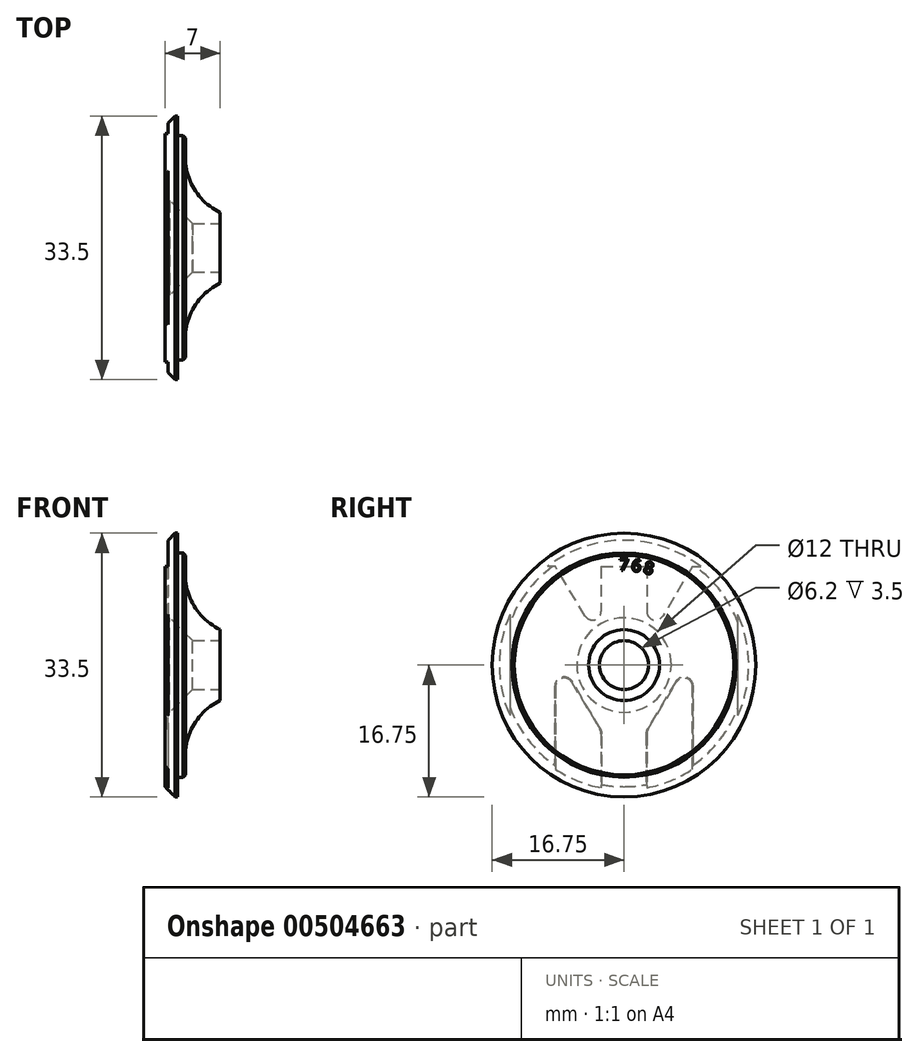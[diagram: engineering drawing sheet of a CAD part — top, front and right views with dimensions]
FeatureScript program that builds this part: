
annotation { "Feature Type Name" : "Feature", "Feature Type Description" : "" }
export const myFeature = defineFeature(function(context is Context, id is Id, definition is map)
    precondition{}
    {
        {
            var Q0;
            Q0=qCreatedBy(makeId("Top.planeOp"),FACE);
            var sketch = newSketch(context, id + "F0", { "sketchPlane" : qUnion([Q0])});
            skLineSegment(sketch, "E0", {"start": v(-4.4, 14.25) * mm, "end": v(-5.4, 14.25) * mm});
            skLineSegment(sketch, "E1", {"start": v(-5.4, 14.25) * mm, "end": v(-5.4, 16.75) * mm});
            skLineSegment(sketch, "E2", {"start": v(0, 0) * mm, "end": v(-7, 0) * mm, "construction": true});
            skLineSegment(sketch, "E3", {"start": v(-3.5, 3.1) * mm, "end": v(0, 3.1) * mm});
            skLineSegment(sketch, "E4", {"start": v(0, 3.1) * mm, "end": v(0, 4.5) * mm});
            skLineSegment(sketch, "E5", {"start": v(-5.4, 16.75) * mm, "end": v(-7, 16.75) * mm});
            skLineSegment(sketch, "E6", {"start": v(-7, 6) * mm, "end": v(-7, 16.75) * mm});
            skLineSegment(sketch, "E7", {"start": v(-6.4, 6) * mm, "end": v(-3.5, 3.1) * mm});
            skLineSegment(sketch, "E8", {"start": v(-7, 6) * mm, "end": v(-6.4, 6) * mm});
            skLineSegment(sketch, "E9", {"start": v(-4.4, 14.25) * mm, "end": v(-4.4, 11.5) * mm});
            skArc(sketch, "E10", {"start": v(-4.4, 11.5) * mm, "mid": v(-3.2, 7.37) * mm, "end": v(0, 4.5) * mm});
            skSolve(sketch);
        }
        {
            var Q0;
            Q0=makeQuery(id+"F0.imprint","IMPRINT",FACE,{"disambiguationData":[TD([[makeQuery(id+"F0.imprint","IMPRINT",EDGE,{"derivedFrom":sQuery(id+"F0.wireOp",EDGE,"E0")}),1.0]])]});
            var Q1;
            Q1=sQuery(id+"F0.wireOp",EDGE,"E2");
            revolve(context, id + "F1", {"entities" : qUnion([Q0]), "axis" : qUnion([Q1]), "revolveType" : RevolveType.FULL});
        }
        {
            var Q0;
            Q0=makeQuery(id+"F1.opRevolve","SWEPT_EDGE",EDGE,{"disambiguationData":[OSD([sQuery(id+"F0.wireOp",EDGE,"E5"),sQuery(id+"F0.wireOp",EDGE,"E6")])]});
            chamfer(context, id + "F2", {"entities" : qUnion([Q0]), "width" : 1.3 * mm, "tangentPropagation" : true});
        }
        {
            var Q0;
            Q0=makeQuery(id+"F1.opRevolve","SWEPT_FACE",FACE,{"disambiguationData":[OSD([sQuery(id+"F0.wireOp",EDGE,"E6")])]});
            var sketch = newSketch(context, id + "F3", { "sketchPlane" : qUnion([Q0])});
            skCircle(sketch, "E11", {"center": v(0, 0) * mm, "radius": 16.75 * mm});
            skLineSegment(sketch, "E12", {"start": v(-2.9, 12.5) * mm, "end": v(-2.9, -16.5) * mm});
            skLineSegment(sketch, "E13.MirrorCS", {"start": v(2.9, 12.5) * mm, "end": v(2.9, -16.5) * mm});
            skLineSegment(sketch, "E14", {"start": v(-8.7, -14.31) * mm, "end": v(-8.7, 1.24) * mm});
            skLineSegment(sketch, "E15", {"start": v(-8.7, 1.24) * mm, "end": v(-2.9, -8.41) * mm});
            skLineSegment(sketch, "E16", {"start": v(2.9, -8.41) * mm, "end": v(8.7, 1.24) * mm});
            skLineSegment(sketch, "E17", {"start": v(8.7, 1.24) * mm, "end": v(8.7, -14.31) * mm});
            skLineSegment(sketch, "E18", {"start": v(-14.5, -8.39) * mm, "end": v(-14.5, 8.39) * mm});
            skLineSegment(sketch, "E19", {"start": v(-8.7, 12.5) * mm, "end": v(-2.9, 2.85) * mm});
            skLineSegment(sketch, "E20", {"start": v(2.9, 2.85) * mm, "end": v(8.7, 12.5) * mm});
            skLineSegment(sketch, "E21", {"start": v(14.5, 8.39) * mm, "end": v(14.5, -8.39) * mm});
            skLineSegment(sketch, "E22", {"start": v(0, 16.75) * mm, "end": v(0, -16.75) * mm, "construction": true});
            skLineSegment(sketch, "E23", {"start": v(2.9, 12.5) * mm, "end": v(-2.9, 12.5) * mm});
            skLineSegment(sketch, "E24", {"start": v(8.7, 1.24) * mm, "end": v(14.5, 1.24) * mm, "construction": true});
            skLineSegment(sketch, "E25", {"start": v(-8.7, 1.24) * mm, "end": v(-14.5, 1.24) * mm, "construction": true});
            skLineSegment(sketch, "E26", {"start": v(-2.9, 2.85) * mm, "end": v(-7.87, -0.14) * mm, "construction": true});
            skLineSegment(sketch, "E27", {"start": v(2.9, -8.41) * mm, "end": v(8.7, -8.41) * mm, "construction": true});
            skLineSegment(sketch, "E28", {"start": v(-8.7, 12.5) * mm, "end": v(-11.15, 12.5) * mm});
            skLineSegment(sketch, "E29", {"start": v(8.7, 12.5) * mm, "end": v(11.15, 12.5) * mm});
            skArc(sketch, "E30", {"start": v(-4.94, 6.25) * mm, "mid": v(-3.7, 5.75) * mm, "end": v(-2.9, 6.81) * mm});
            skArc(sketch, "E31", {"start": v(2.9, 6.81) * mm, "mid": v(3.7, 5.75) * mm, "end": v(4.94, 6.25) * mm});
            skCircle(sketch, "E32.0", {"center": v(0, 0) * mm, "radius": 6 * mm, "construction": true});
            skLineSegment(sketch, "E33", {"start": v(8.7, -11.87) * mm, "end": v(14.5, -11.87) * mm, "construction": true});
            skSolve(sketch);
        }
        {
            var Q0;
            {var subQ8=sQuery(id+"F3.wireOp",EDGE,"E23");Q0=makeQuery(id+"F3.imprint","IMPRINT",FACE,{"disambiguationData":[TD([[makeQuery(id+"F3.imprint","IMPRINT",EDGE,{"derivedFrom":subQ8}),-1.0]])]});}
            var Q1;
            {var subQ0=sQuery(id+"F3.wireOp",EDGE,"E15");Q1=makeQuery(id+"F3.imprint","IMPRINT",FACE,{"disambiguationData":[TD([[makeQuery(id+"F3.imprint","IMPRINT",EDGE,{"derivedFrom":subQ0}),-1.0]])]});}
            var Q2;
            {var subQ0=sQuery(id+"F3.wireOp",EDGE,"E16");Q2=makeQuery(id+"F3.imprint","IMPRINT",FACE,{"disambiguationData":[TD([[makeQuery(id+"F3.imprint","IMPRINT",EDGE,{"derivedFrom":subQ0}),-1.0]])]});}
            var Q3;
            {var subQ0=sQuery(id+"F3.wireOp",EDGE,"E21");var subQ1=sQuery(id+"F0.wireOp",EDGE,"E6");var subQ2=makeQuery(id+"F2.opChamfer","BLEND_EDGE",EDGE,{"blendedFrom":[makeQuery(id+"F1.opRevolve","SWEPT_EDGE",EDGE,{"disambiguationData":[OSD([sQuery(id+"F0.wireOp",EDGE,"E5"),subQ1])]}),makeQuery(id+"F1.opRevolve","SWEPT_FACE",FACE,{"disambiguationData":[OSD([subQ1])]})],"blendedInto":[makeQuery(id+"F1.opRevolve","SWEPT_FACE",FACE,{"disambiguationData":[OSD([subQ1])]})]});var subQ3=makeQuery(id+"F3.imprint","INTERSECT",VERTEX,{"disambiguationData":[OD(0.0)],"derivedFrom":[subQ2,subQ0]});Q3=makeQuery(id+"F3.imprint","IMPRINT",FACE,{"disambiguationData":[TD([[makeQuery(id+"F3.imprint","IMPRINT",EDGE,{"disambiguationData":[TD([[subQ3,-1.0]])],"derivedFrom":subQ0}),1.0]])]});}
            var Q4;
            {var subQ0=sQuery(id+"F3.wireOp",EDGE,"E21");var subQ1=sQuery(id+"F3.wireOp",EDGE,"E11");var subQ2=makeQuery(id+"F3.imprint","INTERSECT",VERTEX,{"disambiguationData":[OD(0.0)],"derivedFrom":[subQ1,subQ0]});Q4=makeQuery(id+"F3.imprint","IMPRINT",FACE,{"disambiguationData":[TD([[makeQuery(id+"F3.imprint","IMPRINT",EDGE,{"disambiguationData":[TD([[subQ2,1.0]])],"derivedFrom":subQ1}),1.0]])]});}
            var Q5;
            {var subQ0=sQuery(id+"F3.wireOp",EDGE,"E18");var subQ1=sQuery(id+"F0.wireOp",EDGE,"E6");var subQ2=makeQuery(id+"F2.opChamfer","BLEND_EDGE",EDGE,{"blendedFrom":[makeQuery(id+"F1.opRevolve","SWEPT_EDGE",EDGE,{"disambiguationData":[OSD([sQuery(id+"F0.wireOp",EDGE,"E5"),subQ1])]}),makeQuery(id+"F1.opRevolve","SWEPT_FACE",FACE,{"disambiguationData":[OSD([subQ1])]})],"blendedInto":[makeQuery(id+"F1.opRevolve","SWEPT_FACE",FACE,{"disambiguationData":[OSD([subQ1])]})]});var subQ3=makeQuery(id+"F3.imprint","INTERSECT",VERTEX,{"disambiguationData":[OD(0.0)],"derivedFrom":[subQ2,subQ0]});Q5=makeQuery(id+"F3.imprint","IMPRINT",FACE,{"disambiguationData":[TD([[makeQuery(id+"F3.imprint","IMPRINT",EDGE,{"disambiguationData":[TD([[subQ3,-1.0]])],"derivedFrom":subQ0}),1.0]])]});}
            var Q6;
            {var subQ0=sQuery(id+"F3.wireOp",EDGE,"E18");var subQ1=sQuery(id+"F3.wireOp",EDGE,"E11");var subQ2=makeQuery(id+"F3.imprint","INTERSECT",VERTEX,{"disambiguationData":[OD(0.0)],"derivedFrom":[subQ1,subQ0]});Q6=makeQuery(id+"F3.imprint","IMPRINT",FACE,{"disambiguationData":[TD([[makeQuery(id+"F3.imprint","IMPRINT",EDGE,{"disambiguationData":[TD([[subQ2,1.0]])],"derivedFrom":subQ1}),1.0]])]});}
            var Q7;
            {var subQ0=sQuery(id+"F3.wireOp",EDGE,"E28");var subQ1=sQuery(id+"F3.wireOp",EDGE,"E11");var subQ2=makeQuery(id+"F3.imprint","INTERSECT",VERTEX,{"derivedFrom":[subQ1,subQ0]});Q7=makeQuery(id+"F3.imprint","IMPRINT",FACE,{"disambiguationData":[TD([[makeQuery(id+"F3.imprint","IMPRINT",EDGE,{"disambiguationData":[TD([[subQ2,1.0]])],"derivedFrom":subQ1}),1.0]])]});}
            var Q8;
            {var subQ0=sQuery(id+"F3.wireOp",EDGE,"E12");var subQ1=sQuery(id+"F3.wireOp",EDGE,"E11");var subQ2=makeQuery(id+"F3.imprint","INTERSECT",VERTEX,{"derivedFrom":[subQ1,subQ0]});Q8=makeQuery(id+"F3.imprint","IMPRINT",FACE,{"disambiguationData":[TD([[makeQuery(id+"F3.imprint","IMPRINT",EDGE,{"disambiguationData":[TD([[subQ2,1.0]])],"derivedFrom":subQ1}),1.0]])]});}
            var Q9;
            {var subQ0=sQuery(id+"F3.wireOp",EDGE,"E13.MirrorCS");var subQ1=sQuery(id+"F3.wireOp",EDGE,"E11");var subQ2=makeQuery(id+"F3.imprint","INTERSECT",VERTEX,{"derivedFrom":[subQ1,subQ0]});Q9=makeQuery(id+"F3.imprint","IMPRINT",FACE,{"disambiguationData":[TD([[makeQuery(id+"F3.imprint","IMPRINT",EDGE,{"disambiguationData":[TD([[subQ2,-1.0]])],"derivedFrom":subQ1}),1.0]])]});}
            extrude(context, id + "F4", {"entities" : qUnion([Q0, Q1, Q2, Q3, Q4, Q5, Q6, Q7, Q8, Q9]), "operationType" : NewBodyOperationType.REMOVE, "oppositeDirection" : true, "depth" : 0.4 * mm, "offsetDistance" : 25 * mm});
        }
        {
            var Q0;
            Q0=makeQuery(id+"F4.boolean.opBoolean","COPY",EDGE,{"derivedFrom":makeQuery(id+"F4.opExtrude","SWEPT_EDGE",EDGE,{"disambiguationData":[OSD([sQuery(id+"F3.wireOp",EDGE,"E14"),sQuery(id+"F3.wireOp",EDGE,"E15")])]})});
            var Q1;
            Q1=makeQuery(id+"F4.boolean.opBoolean","COPY",EDGE,{"derivedFrom":makeQuery(id+"F4.opExtrude","SWEPT_EDGE",EDGE,{"disambiguationData":[OSD([sQuery(id+"F3.wireOp",EDGE,"E16"),sQuery(id+"F3.wireOp",EDGE,"E17")])]})});
            var Q2;
            Q2=makeQuery(id+"F4.boolean.opBoolean","COPY",EDGE,{"derivedFrom":makeQuery(id+"F4.opExtrude","SWEPT_EDGE",EDGE,{"disambiguationData":[OSD([sQuery(id+"F3.wireOp",EDGE,"E12"),sQuery(id+"F3.wireOp",EDGE,"E15")])]})});
            var Q3;
            Q3=makeQuery(id+"F4.boolean.opBoolean","COPY",EDGE,{"derivedFrom":makeQuery(id+"F4.opExtrude","SWEPT_EDGE",EDGE,{"disambiguationData":[OSD([sQuery(id+"F3.wireOp",EDGE,"E13.MirrorCS"),sQuery(id+"F3.wireOp",EDGE,"E16")])]})});
            fillet(context, id + "F5", {"entities" : qUnion([Q0, Q1, Q2, Q3]), "radius" : 1.1 * mm, "tangentPropagation" : true, "allowEdgeOverflow" : false});
        }
        {
            var Q0;
            Q0=makeQuery(id+"F1.opRevolve","SWEPT_FACE",FACE,{"disambiguationData":[OSD([sQuery(id+"F0.wireOp",EDGE,"E9")])]});
            var sketch = newSketch(context, id + "F6", { "sketchPlane" : qUnion([Q0])});
            skCircle(sketch, "E34", {"center": v(0, 0) * mm, "radius": 12 * mm, "construction": true});
            skCircle(sketch, "E35.cCircle", {"center": v(0, 0) * mm, "radius": 11.98 * mm, "construction": true});
            skLineSegment(sketch, "E35.0", {"start": v(-2.98, -11.62) * mm, "end": v(-4.42, -11.16) * mm});
            skLineSegment(sketch, "E35.1", {"start": v(-4.42, -11.16) * mm, "end": v(-5.78, -10.52) * mm});
            skLineSegment(sketch, "E35.2", {"start": v(-5.78, -10.52) * mm, "end": v(-7.05, -9.7) * mm});
            skLineSegment(sketch, "E35.3", {"start": v(-7.05, -9.7) * mm, "end": v(-8.21, -8.75) * mm});
            skLineSegment(sketch, "E35.4", {"start": v(-8.21, -8.75) * mm, "end": v(-9.25, -7.65) * mm});
            skLineSegment(sketch, "E35.5", {"start": v(-9.25, -7.65) * mm, "end": v(-10.13, -6.43) * mm});
            skLineSegment(sketch, "E35.6", {"start": v(-10.13, -6.43) * mm, "end": v(-10.86, -5.1) * mm});
            skLineSegment(sketch, "E35.7", {"start": v(-10.86, -5.1) * mm, "end": v(-11.41, -3.7) * mm});
            skLineSegment(sketch, "E35.8", {"start": v(-11.41, -3.7) * mm, "end": v(-11.79, -2.25) * mm});
            skLineSegment(sketch, "E35.9", {"start": v(-11.79, -2.25) * mm, "end": v(-11.98, -0.75) * mm});
            skLineSegment(sketch, "E35.10", {"start": v(-11.98, -0.75) * mm, "end": v(-11.98, 0.75) * mm});
            skLineSegment(sketch, "E35.11", {"start": v(-11.98, 0.75) * mm, "end": v(-11.79, 2.25) * mm});
            skLineSegment(sketch, "E35.12", {"start": v(-11.79, 2.25) * mm, "end": v(-11.41, 3.7) * mm});
            skLineSegment(sketch, "E35.13", {"start": v(-11.41, 3.7) * mm, "end": v(-10.86, 5.1) * mm});
            skLineSegment(sketch, "E35.14", {"start": v(-10.86, 5.1) * mm, "end": v(-10.13, 6.43) * mm});
            skLineSegment(sketch, "E35.15", {"start": v(-10.13, 6.43) * mm, "end": v(-9.25, 7.65) * mm});
            skLineSegment(sketch, "E35.16", {"start": v(-9.25, 7.65) * mm, "end": v(-8.21, 8.75) * mm});
            skLineSegment(sketch, "E35.17", {"start": v(-8.21, 8.75) * mm, "end": v(-7.05, 9.7) * mm});
            skLineSegment(sketch, "E35.18", {"start": v(-7.05, 9.7) * mm, "end": v(-5.78, 10.52) * mm});
            skLineSegment(sketch, "E35.19", {"start": v(-5.78, 10.52) * mm, "end": v(-4.42, 11.16) * mm});
            skLineSegment(sketch, "E35.20", {"start": v(-4.42, 11.16) * mm, "end": v(-2.98, 11.62) * mm});
            skLineSegment(sketch, "E35.21", {"start": v(-2.98, 11.62) * mm, "end": v(-1.5, 11.9) * mm});
            skLineSegment(sketch, "E35.22", {"start": v(-1.5, 11.9) * mm, "end": v(0, 12) * mm});
            skLineSegment(sketch, "E35.23", {"start": v(0, 12) * mm, "end": v(1.5, 11.9) * mm});
            skLineSegment(sketch, "E35.24", {"start": v(1.5, 11.9) * mm, "end": v(2.98, 11.62) * mm});
            skLineSegment(sketch, "E35.25", {"start": v(2.98, 11.62) * mm, "end": v(4.42, 11.16) * mm});
            skLineSegment(sketch, "E35.26", {"start": v(4.42, 11.16) * mm, "end": v(5.78, 10.52) * mm});
            skLineSegment(sketch, "E35.27", {"start": v(5.78, 10.52) * mm, "end": v(7.05, 9.7) * mm});
            skLineSegment(sketch, "E35.28", {"start": v(7.05, 9.7) * mm, "end": v(8.21, 8.75) * mm});
            skLineSegment(sketch, "E35.29", {"start": v(8.21, 8.75) * mm, "end": v(9.25, 7.65) * mm});
            skLineSegment(sketch, "E35.30", {"start": v(9.25, 7.65) * mm, "end": v(10.13, 6.43) * mm});
            skLineSegment(sketch, "E35.31", {"start": v(10.13, 6.43) * mm, "end": v(10.86, 5.1) * mm});
            skLineSegment(sketch, "E35.32", {"start": v(10.86, 5.1) * mm, "end": v(11.41, 3.7) * mm});
            skLineSegment(sketch, "E35.33", {"start": v(11.41, 3.7) * mm, "end": v(11.79, 2.25) * mm});
            skLineSegment(sketch, "E35.34", {"start": v(11.79, 2.25) * mm, "end": v(11.98, 0.75) * mm});
            skLineSegment(sketch, "E35.35", {"start": v(11.98, 0.75) * mm, "end": v(11.98, -0.75) * mm});
            skLineSegment(sketch, "E35.36", {"start": v(11.98, -0.75) * mm, "end": v(11.79, -2.25) * mm});
            skLineSegment(sketch, "E35.37", {"start": v(11.79, -2.25) * mm, "end": v(11.41, -3.7) * mm});
            skLineSegment(sketch, "E35.38", {"start": v(11.41, -3.7) * mm, "end": v(10.86, -5.1) * mm});
            skLineSegment(sketch, "E35.39", {"start": v(10.86, -5.1) * mm, "end": v(10.13, -6.43) * mm});
            skLineSegment(sketch, "E35.40", {"start": v(10.13, -6.43) * mm, "end": v(9.25, -7.65) * mm});
            skLineSegment(sketch, "E35.41", {"start": v(9.25, -7.65) * mm, "end": v(8.21, -8.75) * mm});
            skLineSegment(sketch, "E35.42", {"start": v(8.21, -8.75) * mm, "end": v(7.05, -9.7) * mm});
            skLineSegment(sketch, "E35.43", {"start": v(7.05, -9.7) * mm, "end": v(5.78, -10.52) * mm});
            skLineSegment(sketch, "E35.44", {"start": v(5.78, -10.52) * mm, "end": v(4.42, -11.16) * mm});
            skLineSegment(sketch, "E35.45", {"start": v(4.42, -11.16) * mm, "end": v(2.98, -11.62) * mm});
            skLineSegment(sketch, "E35.46", {"start": v(2.98, -11.62) * mm, "end": v(1.5, -11.9) * mm});
            skLineSegment(sketch, "E35.47", {"start": v(1.5, -11.9) * mm, "end": v(0, -12) * mm});
            skLineSegment(sketch, "E35.48", {"start": v(0, -12) * mm, "end": v(-1.5, -11.9) * mm});
            skLineSegment(sketch, "E35.49", {"start": v(-1.5, -11.9) * mm, "end": v(-2.98, -11.62) * mm});
            skPoint(sketch, "E35.0.midPoint", {"position": v(-3.7, -11.4) * mm});
            skLineSegment(sketch, "E36", {"start": v(0, 0) * mm, "end": v(0, 12) * mm, "construction": true});
            skLineSegment(sketch, "E37", {"start": v(0, 0) * mm, "end": v(1.5, 11.9) * mm, "construction": true});
            skLineSegment(sketch, "E38", {"start": v(0, 0) * mm, "end": v(2.98, 11.62) * mm, "construction": true});
            skText(sketch, "E39", { "text": "7", "fontName": "OpenSans-Regular.ttf"});
            skText(sketch, "E40", { "text": "8", "fontName": "OpenSans-Regular.ttf"});
            skText(sketch, "E41", { "text": "6", "fontName": "OpenSans-Regular.ttf"});
            skText(sketch, "E42", { "text": "-", "fontName": "OpenSans-Regular.ttf"});
            skLineSegment(sketch, "E43", {"start": v(0, 0) * mm, "end": v(5.78, 10.52) * mm, "construction": true});
            skLineSegment(sketch, "E44", {"start": v(8.21, 8.75) * mm, "end": v(0, 0) * mm, "construction": true});
            skCircle(sketch, "E45.0", {"center": v(0, 0) * mm, "radius": 11.5 * mm, "construction": true});
            skCircle(sketch, "E46.0", {"center": v(0, 0) * mm, "radius": 14.25 * mm, "construction": true});
            const initialGuessF6  = {"E39": [-0.00061, 0.012, 1, 0, 0.0015], "E40": [0.0024, 0.01177, 0.96858, -0.24869, 0.0015], "E41": [0.0009, 0.01198, 0.99211, -0.12533, 0.0015], "E42": [0.00547, 0.01069, 0.8763, -0.48175, 0.0015]};
            skSetInitialGuess(sketch, initialGuessF6);
            skSolve(sketch);
        }
        {
            var Q0;
            Q0=makeQuery(id+"F6.imprint","IMPRINT",FACE,{"disambiguationData":[TD([[makeQuery(id+"F6.imprint","IMPRINT",EDGE,{"derivedFrom":sQuery(id+"F6.wireOp",EDGE,"E39.sketch_text.stroke-0")}),-1.0]])]});
            var Q1;
            Q1=makeQuery(id+"F6.imprint","IMPRINT",FACE,{"disambiguationData":[TD([[makeQuery(id+"F6.imprint","IMPRINT",EDGE,{"derivedFrom":sQuery(id+"F6.wireOp",EDGE,"E41.sketch_text.stroke-0")}),-1.0]])]});
            var Q2;
            Q2=makeQuery(id+"F6.imprint","IMPRINT",FACE,{"disambiguationData":[TD([[makeQuery(id+"F6.imprint","IMPRINT",EDGE,{"derivedFrom":sQuery(id+"F6.wireOp",EDGE,"E40.sketch_text.stroke-0")}),-1.0]])]});
            extrude(context, id + "F7", {"entities" : qUnion([Q0, Q1, Q2]), "operationType" : NewBodyOperationType.REMOVE, "oppositeDirection" : true, "depth" : 0.05 * mm, "offsetDistance" : 25 * mm});
        }
        {
            var Q0;
            Q0=makeQuery(id+"F1.opRevolve","SWEPT_EDGE",EDGE,{"disambiguationData":[OSD([sQuery(id+"F0.wireOp",EDGE,"E0"),sQuery(id+"F0.wireOp",EDGE,"E9")])]});
            chamfer(context, id + "F8", {"entities" : qUnion([Q0]), "width" : 0.3 * mm, "tangentPropagation" : true});
        }
        {
            var Q0;
            Q0=makeQuery(id+"F4.boolean.opBoolean","COPY",EDGE,{"derivedFrom":makeQuery(id+"F4.opExtrude","CAP_EDGE",EDGE,{"disambiguationData":[OSD([sQuery(id+"F3.wireOp",EDGE,"E14")])],"isStart":true})});
            var Q1;
            Q1=makeQuery(id+"F5.opFillet","BLEND_EDGE",EDGE,{"blendedFrom":[makeQuery(id+"F4.boolean.opBoolean","COPY",EDGE,{"derivedFrom":makeQuery(id+"F4.opExtrude","SWEPT_EDGE",EDGE,{"disambiguationData":[OSD([sQuery(id+"F3.wireOp",EDGE,"E14"),sQuery(id+"F3.wireOp",EDGE,"E15")])]})}),makeQuery(id+"F1.opRevolve","SWEPT_FACE",FACE,{"disambiguationData":[OSD([sQuery(id+"F0.wireOp",EDGE,"E6")])]})],"blendedInto":[makeQuery(id+"F1.opRevolve","SWEPT_FACE",FACE,{"disambiguationData":[OSD([sQuery(id+"F0.wireOp",EDGE,"E6")])]})]});
            var Q2;
            {var subQ0=sQuery(id+"F3.wireOp",EDGE,"E13.MirrorCS");Q2=makeQuery(id+"F4.boolean.opBoolean","COPY",EDGE,{"derivedFrom":makeQuery(id+"F4.opExtrude","CAP_EDGE",EDGE,{"disambiguationData":[OSD([subQ0]),TDD([makeQuery(id+"F3.imprint","IMPRINT",EDGE,{"disambiguationData":[TD([[makeQuery(id+"F3.imprint","INTERSECT",VERTEX,{"derivedFrom":[subQ0,sQuery(id+"F3.wireOp",EDGE,"E16")]}),-1.0]])],"derivedFrom":subQ0}),makeQuery(id+"F3.imprint","IMPRINT",EDGE,{"disambiguationData":[TD([[makeQuery(id+"F3.imprint","INTERSECT",VERTEX,{"derivedFrom":[sQuery(id+"F3.wireOp",EDGE,"E11"),subQ0]}),1.0]])],"derivedFrom":subQ0})])],"isStart":true})});}
            var Q3;
            Q3=makeQuery(id+"F5.opFillet","BLEND_EDGE",EDGE,{"blendedFrom":[makeQuery(id+"F4.boolean.opBoolean","COPY",EDGE,{"derivedFrom":makeQuery(id+"F4.opExtrude","SWEPT_EDGE",EDGE,{"disambiguationData":[OSD([sQuery(id+"F3.wireOp",EDGE,"E13.MirrorCS"),sQuery(id+"F3.wireOp",EDGE,"E16")])]})}),makeQuery(id+"F1.opRevolve","SWEPT_FACE",FACE,{"disambiguationData":[OSD([sQuery(id+"F0.wireOp",EDGE,"E6")])]})],"blendedInto":[makeQuery(id+"F1.opRevolve","SWEPT_FACE",FACE,{"disambiguationData":[OSD([sQuery(id+"F0.wireOp",EDGE,"E6")])]})]});
            var Q4;
            Q4=makeQuery(id+"F4.boolean.opBoolean","COPY",EDGE,{"derivedFrom":makeQuery(id+"F4.opExtrude","CAP_EDGE",EDGE,{"disambiguationData":[OSD([sQuery(id+"F3.wireOp",EDGE,"E16")])],"isStart":true})});
            var Q5;
            Q5=makeQuery(id+"F5.opFillet","BLEND_EDGE",EDGE,{"blendedFrom":[makeQuery(id+"F4.boolean.opBoolean","COPY",EDGE,{"derivedFrom":makeQuery(id+"F4.opExtrude","SWEPT_EDGE",EDGE,{"disambiguationData":[OSD([sQuery(id+"F3.wireOp",EDGE,"E16"),sQuery(id+"F3.wireOp",EDGE,"E17")])]})}),makeQuery(id+"F1.opRevolve","SWEPT_FACE",FACE,{"disambiguationData":[OSD([sQuery(id+"F0.wireOp",EDGE,"E6")])]})],"blendedInto":[makeQuery(id+"F1.opRevolve","SWEPT_FACE",FACE,{"disambiguationData":[OSD([sQuery(id+"F0.wireOp",EDGE,"E6")])]})]});
            var Q6;
            Q6=makeQuery(id+"F4.boolean.opBoolean","COPY",EDGE,{"derivedFrom":makeQuery(id+"F4.opExtrude","CAP_EDGE",EDGE,{"disambiguationData":[OSD([sQuery(id+"F3.wireOp",EDGE,"E21")])],"isStart":true})});
            var Q7;
            Q7=makeQuery(id+"F4.boolean.opBoolean","COPY",EDGE,{"derivedFrom":makeQuery(id+"F4.opExtrude","CAP_EDGE",EDGE,{"disambiguationData":[OSD([sQuery(id+"F3.wireOp",EDGE,"E19")])],"isStart":true})});
            var Q8;
            Q8=makeQuery(id+"F4.boolean.opBoolean","COPY",EDGE,{"derivedFrom":makeQuery(id+"F4.opExtrude","CAP_EDGE",EDGE,{"disambiguationData":[OSD([sQuery(id+"F3.wireOp",EDGE,"E30")])],"isStart":true})});
            var Q9;
            {var subQ0=sQuery(id+"F3.wireOp",EDGE,"E12");Q9=makeQuery(id+"F4.boolean.opBoolean","COPY",EDGE,{"derivedFrom":makeQuery(id+"F4.opExtrude","CAP_EDGE",EDGE,{"disambiguationData":[OSD([subQ0]),TDD([makeQuery(id+"F3.imprint","IMPRINT",EDGE,{"disambiguationData":[TD([[makeQuery(id+"F3.imprint","INTERSECT",VERTEX,{"derivedFrom":[subQ0,sQuery(id+"F3.wireOp",EDGE,"E23")]}),-1.0]])],"derivedFrom":subQ0})])],"isStart":true})});}
            var Q10;
            {var subQ0=sQuery(id+"F3.wireOp",EDGE,"E13.MirrorCS");Q10=makeQuery(id+"F4.boolean.opBoolean","COPY",EDGE,{"derivedFrom":makeQuery(id+"F4.opExtrude","CAP_EDGE",EDGE,{"disambiguationData":[OSD([subQ0]),TDD([makeQuery(id+"F3.imprint","IMPRINT",EDGE,{"disambiguationData":[TD([[makeQuery(id+"F3.imprint","INTERSECT",VERTEX,{"derivedFrom":[subQ0,sQuery(id+"F3.wireOp",EDGE,"E23")]}),-1.0]])],"derivedFrom":subQ0})])],"isStart":true})});}
            var Q11;
            Q11=makeQuery(id+"F4.boolean.opBoolean","COPY",EDGE,{"derivedFrom":makeQuery(id+"F4.opExtrude","CAP_EDGE",EDGE,{"disambiguationData":[OSD([sQuery(id+"F3.wireOp",EDGE,"E31")])],"isStart":true})});
            var Q12;
            Q12=makeQuery(id+"F4.boolean.opBoolean","COPY",EDGE,{"derivedFrom":makeQuery(id+"F4.opExtrude","CAP_EDGE",EDGE,{"disambiguationData":[OSD([sQuery(id+"F3.wireOp",EDGE,"E20")])],"isStart":true})});
            var Q13;
            Q13=makeQuery(id+"F4.boolean.opBoolean","COPY",EDGE,{"derivedFrom":makeQuery(id+"F4.opExtrude","CAP_EDGE",EDGE,{"disambiguationData":[OSD([sQuery(id+"F3.wireOp",EDGE,"E15")])],"isStart":true})});
            var Q14;
            Q14=makeQuery(id+"F5.opFillet","BLEND_EDGE",EDGE,{"blendedFrom":[makeQuery(id+"F4.boolean.opBoolean","COPY",EDGE,{"derivedFrom":makeQuery(id+"F4.opExtrude","SWEPT_EDGE",EDGE,{"disambiguationData":[OSD([sQuery(id+"F3.wireOp",EDGE,"E12"),sQuery(id+"F3.wireOp",EDGE,"E15")])]})}),makeQuery(id+"F1.opRevolve","SWEPT_FACE",FACE,{"disambiguationData":[OSD([sQuery(id+"F0.wireOp",EDGE,"E6")])]})],"blendedInto":[makeQuery(id+"F1.opRevolve","SWEPT_FACE",FACE,{"disambiguationData":[OSD([sQuery(id+"F0.wireOp",EDGE,"E6")])]})]});
            var Q15;
            {var subQ0=sQuery(id+"F3.wireOp",EDGE,"E12");Q15=makeQuery(id+"F4.boolean.opBoolean","COPY",EDGE,{"derivedFrom":makeQuery(id+"F4.opExtrude","CAP_EDGE",EDGE,{"disambiguationData":[OSD([subQ0]),TDD([makeQuery(id+"F3.imprint","IMPRINT",EDGE,{"disambiguationData":[TD([[makeQuery(id+"F3.imprint","INTERSECT",VERTEX,{"derivedFrom":[subQ0,sQuery(id+"F3.wireOp",EDGE,"E15")]}),-1.0]])],"derivedFrom":subQ0}),makeQuery(id+"F3.imprint","IMPRINT",EDGE,{"disambiguationData":[TD([[makeQuery(id+"F3.imprint","INTERSECT",VERTEX,{"derivedFrom":[sQuery(id+"F3.wireOp",EDGE,"E11"),subQ0]}),1.0]])],"derivedFrom":subQ0})])],"isStart":true})});}
            var Q16;
            Q16=makeQuery(id+"F4.boolean.opBoolean","COPY",EDGE,{"derivedFrom":makeQuery(id+"F4.opExtrude","CAP_EDGE",EDGE,{"disambiguationData":[OSD([sQuery(id+"F3.wireOp",EDGE,"E17")])],"isStart":true})});
            var Q17;
            Q17=makeQuery(id+"F4.boolean.opBoolean","COPY",EDGE,{"derivedFrom":makeQuery(id+"F4.opExtrude","CAP_EDGE",EDGE,{"disambiguationData":[OSD([sQuery(id+"F3.wireOp",EDGE,"E23")])],"isStart":true})});
            var Q18;
            Q18=makeQuery(id+"F4.boolean.opBoolean","COPY",EDGE,{"derivedFrom":makeQuery(id+"F4.opExtrude","CAP_EDGE",EDGE,{"disambiguationData":[OSD([sQuery(id+"F3.wireOp",EDGE,"E28")])],"isStart":true})});
            var Q19;
            Q19=makeQuery(id+"F4.boolean.opBoolean","COPY",EDGE,{"derivedFrom":makeQuery(id+"F4.opExtrude","CAP_EDGE",EDGE,{"disambiguationData":[OSD([sQuery(id+"F3.wireOp",EDGE,"E29")])],"isStart":true})});
            var Q20;
            Q20=makeQuery(id+"F4.boolean.opBoolean","COPY",EDGE,{"derivedFrom":makeQuery(id+"F4.opExtrude","CAP_EDGE",EDGE,{"disambiguationData":[OSD([sQuery(id+"F3.wireOp",EDGE,"E18")])],"isStart":true})});
            chamfer(context, id + "F9", {"entities" : qUnion([Q0, Q1, Q2, Q3, Q4, Q5, Q6, Q7, Q8, Q9, Q10, Q11, Q12, Q13, Q14, Q15, Q16, Q17, Q18, Q19, Q20]), "width" : 0.1 * mm, "tangentPropagation" : true});
        }
    });
